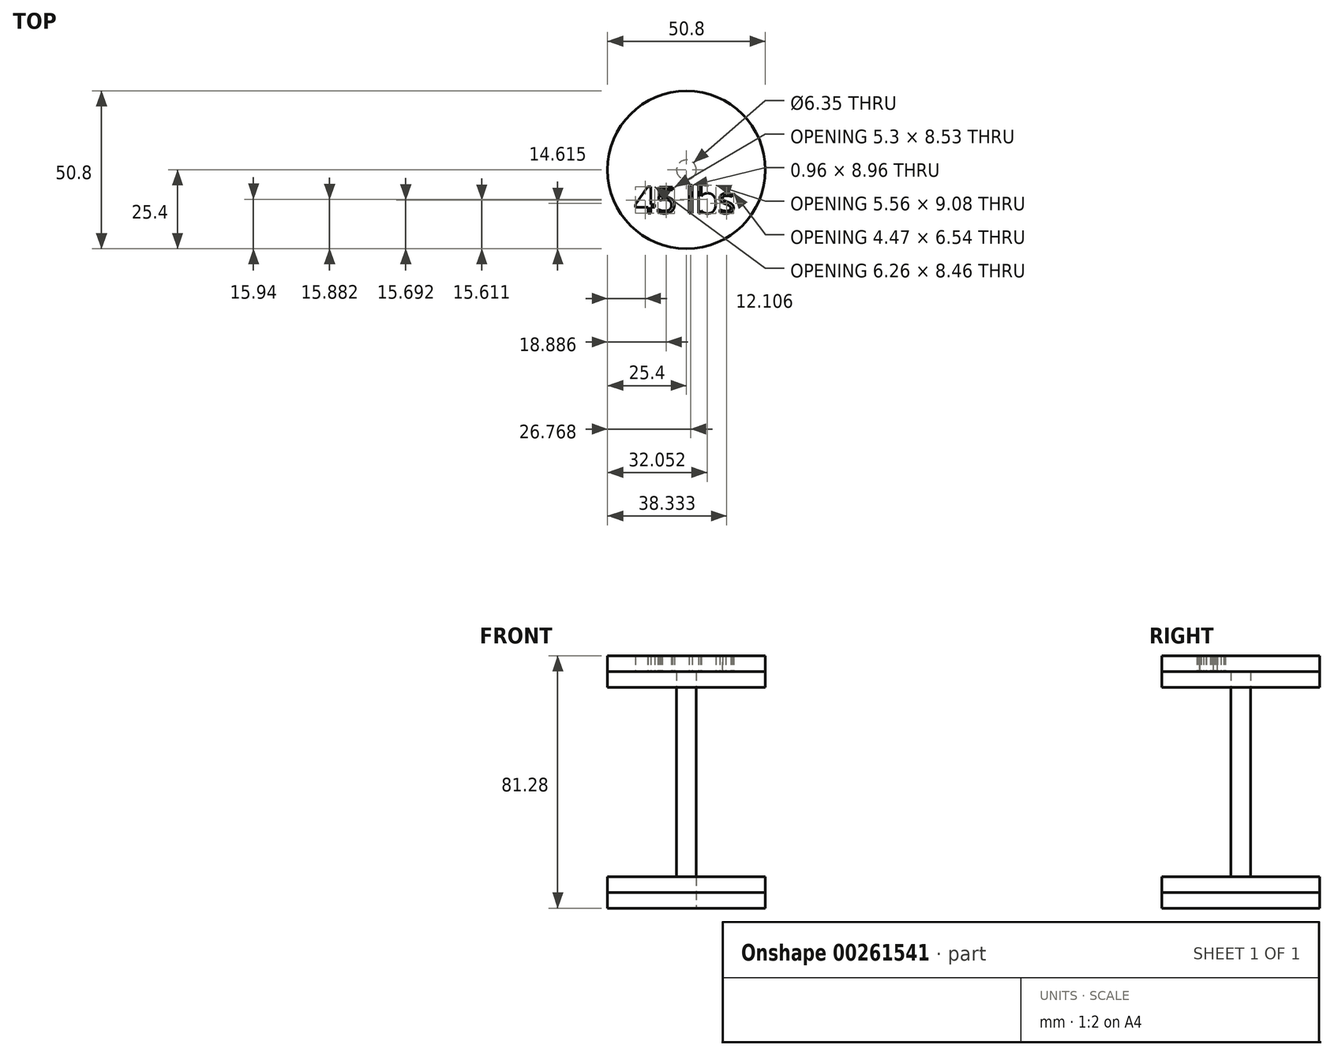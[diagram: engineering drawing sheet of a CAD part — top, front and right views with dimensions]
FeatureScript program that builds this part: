
annotation { "Feature Type Name" : "Feature", "Feature Type Description" : "" }
export const myFeature = defineFeature(function(context is Context, id is Id, definition is map)
    precondition{}
    {
        {
            var Q0;
            Q0=qCreatedBy(makeId("Top.planeOp"),FACE);
            var sketch = newSketch(context, id + "F0", { "sketchPlane" : qUnion([Q0])});
            skCircle(sketch, "E0", {"center": v(0, 0) * mm, "radius": 25.4 * mm});
            skSolve(sketch);
        }
        {
            var Q0;
            Q0 = qSketchRegion(id + "F0", true);
            extrude(context, id + "F1", {"entities" : qUnion([Q0]), "depth" : 5.08 * mm});
        }
        {
            var Q0;
            Q0=sQuery(id+"F0.wireOp",VERTEX,"E0.center");
            var Q1;
            Q1=makeQuery(id+"F1.opExtrude","SWEPT_BODY",BODY,{"disambiguationData":[OSD([sQuery(id+"F0.wireOp",EDGE,"E0")])]});
            hole(context, id + "F2", {"style" : HoleStyle.SIMPLE, "endStyle" : HoleEndStyle.THROUGH, "oppositeDirection" : true, "holeDiameter" : 6.35 * mm, "tappedDepth" : 12.7 * mm, "tapClearance" : 3, "locations" : qUnion([Q0]), "scope" : qUnion([Q1])});
        }
        {
            var Q0;
            Q0=qCreatedBy(makeId("Top.planeOp"),FACE);
            var sketch = newSketch(context, id + "F3", { "sketchPlane" : qUnion([Q0])});
            skCircle(sketch, "E1", {"center": v(0, 0) * mm, "radius": 3.17 * mm});
            skSolve(sketch);
        }
        {
            var Q0;
            Q0 = qSketchRegion(id + "F3", true);
            extrude(context, id + "F4", {"entities" : qUnion([Q0]), "depth" : 76.2 * mm});
        }
        {
            var Q0;
            Q0=qCreatedBy(makeId("Top.planeOp"),FACE);
            var sketch = newSketch(context, id + "F5", { "sketchPlane" : qUnion([Q0])});
            skCircle(sketch, "E2", {"center": v(0, 0) * mm, "radius": 25.4 * mm});
            skText(sketch, "E3", { "text": "45 lbs", "fontName": "OpenSans-Regular.ttf"});
            const initialGuessF5  = {"E3": [-0.01667, -0.01394, 1, 0, 0.00849]};
            skSetInitialGuess(sketch, initialGuessF5);
            skSolve(sketch);
        }
        {
            var Q0;
            Q0 = qSketchRegion(id + "F5", true);
            extrude(context, id + "F6", {"entities" : qUnion([Q0]), "depth" : 5.08 * mm});
        }
        {
            var Q0;
            Q0=makeQuery(id+"F6.opExtrude","SWEPT_BODY",BODY,{"disambiguationData":[OSD([sQuery(id+"F5.wireOp",EDGE,"E2")])]});
            transform(context, id + "F7", {"entities" : qUnion([Q0]), "transformType" : TransformType.TRANSLATION_3D, "dx" : 0 * mm, "dy" : 0 * mm, "dz" : 76.2 * mm, "makeCopy" : false});
        }
        {
            var Q0;
            Q0=qCreatedBy(makeId("Top.planeOp"),FACE);
            var sketch = newSketch(context, id + "F8", { "sketchPlane" : qUnion([Q0])});
            skCircle(sketch, "E4", {"center": v(0, 0) * mm, "radius": 25.4 * mm});
            skSolve(sketch);
        }
        {
            var Q0;
            Q0 = qSketchRegion(id + "F8", true);
            extrude(context, id + "F9", {"entities" : qUnion([Q0]), "depth" : 5.08 * mm});
        }
        {
            var Q0;
            Q0=makeQuery(id+"F9.opExtrude","SWEPT_BODY",BODY,{"disambiguationData":[OSD([sQuery(id+"F8.wireOp",EDGE,"E4")])]});
            var Q1;
            Q1=makeQuery(id+"F4.opExtrude","SWEPT_FACE",FACE,{"disambiguationData":[OSD([sQuery(id+"F3.wireOp",EDGE,"E1")])]});
            transform(context, id + "F10", {"entities" : qUnion([Q0]), "transformType" : TransformType.TRANSLATION_DISTANCE, "transformDirection" : qUnion([Q1]), "distance" : 5.08 * mm, "oppositeDirection" : true, "makeCopy" : false});
        }
        {
            var Q0;
            Q0=qCreatedBy(makeId("Top.planeOp"),FACE);
            var sketch = newSketch(context, id + "F11", { "sketchPlane" : qUnion([Q0])});
            skCircle(sketch, "E5", {"center": v(0, 0) * mm, "radius": 25.4 * mm});
            skSolve(sketch);
        }
        {
            var Q0;
            Q0 = qSketchRegion(id + "F11", true);
            extrude(context, id + "F12", {"entities" : qUnion([Q0]), "depth" : 5.08 * mm});
        }
        {
            var Q0;
            Q0=makeQuery(id+"F1.opExtrude","SWEPT_BODY",BODY,{"disambiguationData":[OSD([sQuery(id+"F0.wireOp",EDGE,"E0")])]});
            var Q1;
            Q1=makeQuery(id+"F4.opExtrude","SWEPT_FACE",FACE,{"disambiguationData":[OSD([sQuery(id+"F3.wireOp",EDGE,"E1")])]});
            transform(context, id + "F13", {"entities" : qUnion([Q0]), "transformType" : TransformType.TRANSLATION_DISTANCE, "transformDirection" : qUnion([Q1]), "distance" : 71.12 * mm, "oppositeDirection" : true, "makeCopy" : false});
        }
    });
